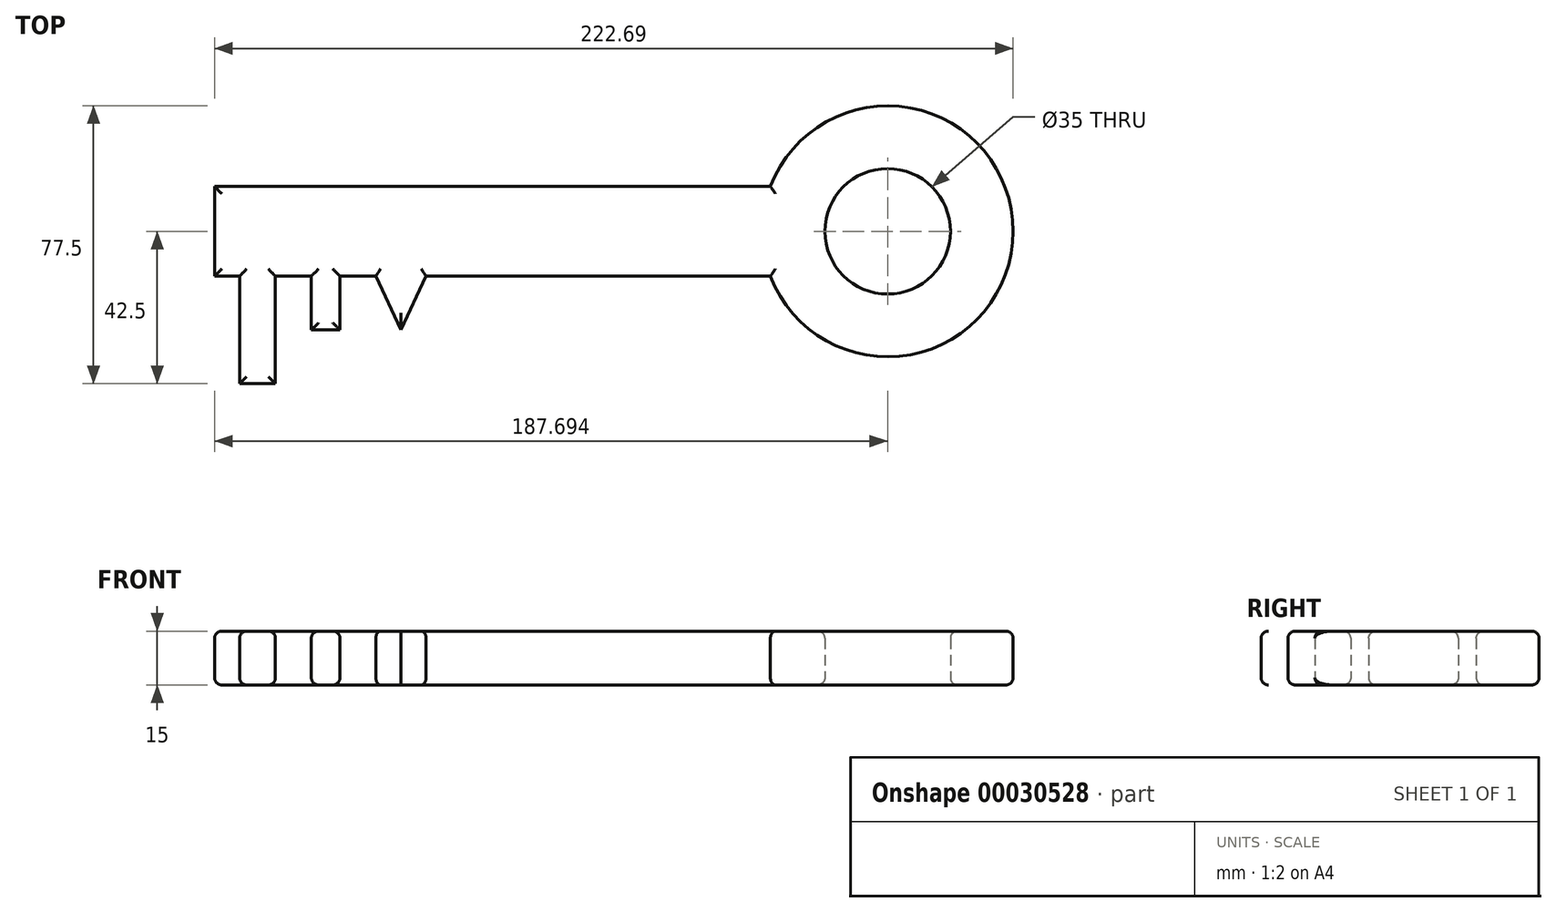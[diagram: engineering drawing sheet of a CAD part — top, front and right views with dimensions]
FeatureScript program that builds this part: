
annotation { "Feature Type Name" : "Feature", "Feature Type Description" : "" }
export const myFeature = defineFeature(function(context is Context, id is Id, definition is map)
    precondition{}
    {
        {
            var Q0;
            Q0=qCreatedBy(makeId("Top.planeOp"),FACE);
            var sketch = newSketch(context, id + "F0", { "sketchPlane" : qUnion([Q0])});
            skLineSegment(sketch, "E0.bottom", {"start": v(20.1, 15) * mm, "end": v(-75.93, 15) * mm});
            skLineSegment(sketch, "E0.top", {"start": v(20.1, 40) * mm, "end": v(-134.9, 40) * mm});
            skLineSegment(sketch, "E0.right", {"start": v(-134.9, 15) * mm, "end": v(-134.9, 40) * mm});
            skLineSegment(sketch, "E1.top", {"start": v(-117.93, -15) * mm, "end": v(-127.93, -15) * mm});
            skLineSegment(sketch, "E1.left", {"start": v(-117.93, 15) * mm, "end": v(-117.93, -15) * mm});
            skLineSegment(sketch, "E1.right", {"start": v(-127.93, 15) * mm, "end": v(-127.93, -15) * mm});
            skLineSegment(sketch, "E2.top", {"start": v(-107.93, 0) * mm, "end": v(-99.93, 0) * mm});
            skLineSegment(sketch, "E2.left", {"start": v(-107.93, 15) * mm, "end": v(-107.93, 0) * mm});
            skLineSegment(sketch, "E2.right", {"start": v(-99.93, 15) * mm, "end": v(-99.93, 0) * mm});
            skLineSegment(sketch, "E3", {"start": v(-89.93, 15) * mm, "end": v(-82.93, 0) * mm});
            skLineSegment(sketch, "E4", {"start": v(-82.93, 0) * mm, "end": v(-75.93, 15) * mm});
            skArc(sketch, "E5", {"start": v(20.1, 15) * mm, "mid": v(87.8, 27.5) * mm, "end": v(20.1, 40) * mm});
            skCircle(sketch, "E6", {"center": v(52.8, 27.5) * mm, "radius": 17.5 * mm});
            skLineSegment(sketch, "E7", {"start": v(-134.9, 27.5) * mm, "end": v(52.8, 27.5) * mm, "construction": true});
            skLineSegment(sketch, "E8.trimOffspring", {"start": v(-107.93, 15) * mm, "end": v(-117.93, 15) * mm});
            skLineSegment(sketch, "E9.trimOffspring", {"start": v(-89.93, 15) * mm, "end": v(-99.93, 15) * mm});
            skLineSegment(sketch, "E10.trimOffspring", {"start": v(-127.93, 15) * mm, "end": v(-134.9, 15) * mm});
            skSolve(sketch);
        }
        {
            var Q0;
            Q0 = qSketchRegion(id + "F0", true);
            extrude(context, id + "F1", {"entities" : qUnion([Q0]), "depth" : 15 * mm});
        }
        {
            var Q0;
            Q0=makeQuery(id+"F1.opExtrude","CAP_FACE",FACE,{"disambiguationData":[OSD([sQuery(id+"F0.wireOp",EDGE,"E0.bottom"),sQuery(id+"F0.wireOp",EDGE,"E0.top"),sQuery(id+"F0.wireOp",EDGE,"E0.right"),sQuery(id+"F0.wireOp",EDGE,"E1.top"),sQuery(id+"F0.wireOp",EDGE,"E1.left"),sQuery(id+"F0.wireOp",EDGE,"E1.right"),sQuery(id+"F0.wireOp",EDGE,"E2.top"),sQuery(id+"F0.wireOp",EDGE,"E2.left"),sQuery(id+"F0.wireOp",EDGE,"E2.right"),sQuery(id+"F0.wireOp",EDGE,"E3"),sQuery(id+"F0.wireOp",EDGE,"E4"),sQuery(id+"F0.wireOp",EDGE,"E5"),sQuery(id+"F0.wireOp",EDGE,"E6"),sQuery(id+"F0.wireOp",EDGE,"E8.trimOffspring"),sQuery(id+"F0.wireOp",EDGE,"E9.trimOffspring"),sQuery(id+"F0.wireOp",EDGE,"E10.trimOffspring")])],"isStart":false});
            fillet(context, id + "F2", {"entities" : qUnion([Q0]), "radius" : 2 * mm, "tangentPropagation" : true, "allowEdgeOverflow" : false});
        }
        {
            var Q0;
            Q0=makeQuery(id+"F1.opExtrude","CAP_FACE",FACE,{"disambiguationData":[OSD([sQuery(id+"F0.wireOp",EDGE,"E0.bottom"),sQuery(id+"F0.wireOp",EDGE,"E0.top"),sQuery(id+"F0.wireOp",EDGE,"E0.right"),sQuery(id+"F0.wireOp",EDGE,"E1.top"),sQuery(id+"F0.wireOp",EDGE,"E1.left"),sQuery(id+"F0.wireOp",EDGE,"E1.right"),sQuery(id+"F0.wireOp",EDGE,"E2.top"),sQuery(id+"F0.wireOp",EDGE,"E2.left"),sQuery(id+"F0.wireOp",EDGE,"E2.right"),sQuery(id+"F0.wireOp",EDGE,"E3"),sQuery(id+"F0.wireOp",EDGE,"E4"),sQuery(id+"F0.wireOp",EDGE,"E5"),sQuery(id+"F0.wireOp",EDGE,"E6"),sQuery(id+"F0.wireOp",EDGE,"E8.trimOffspring"),sQuery(id+"F0.wireOp",EDGE,"E9.trimOffspring"),sQuery(id+"F0.wireOp",EDGE,"E10.trimOffspring")])],"isStart":true});
            fillet(context, id + "F3", {"entities" : qUnion([Q0]), "radius" : 2 * mm, "tangentPropagation" : true, "allowEdgeOverflow" : false});
        }
    });
